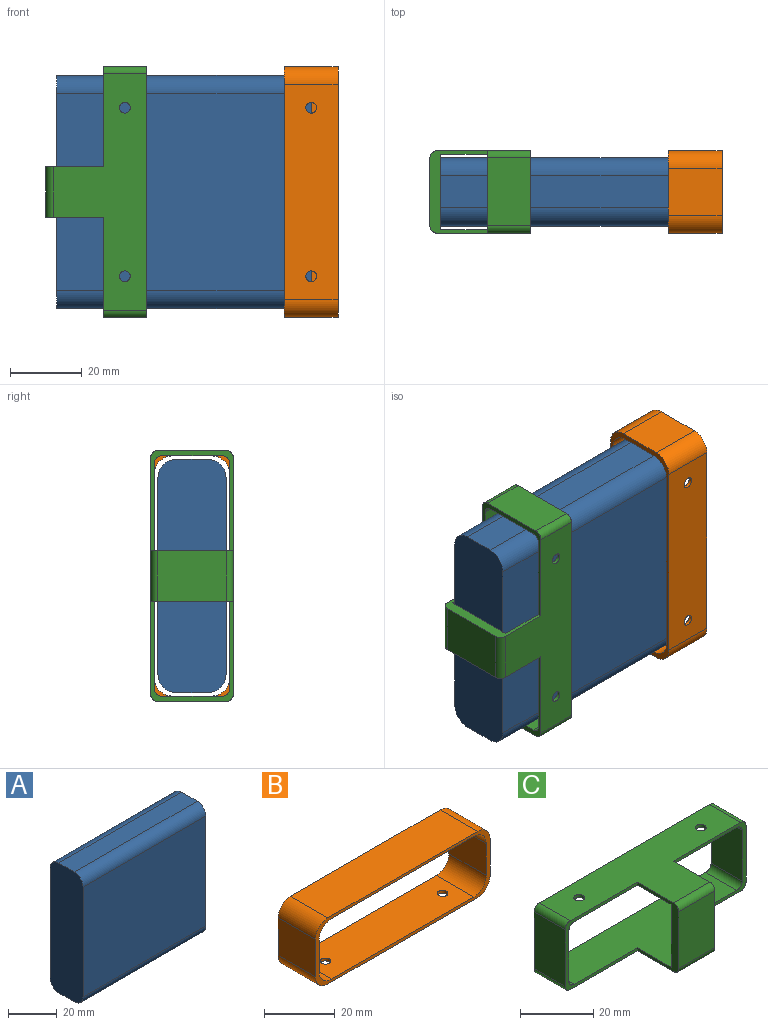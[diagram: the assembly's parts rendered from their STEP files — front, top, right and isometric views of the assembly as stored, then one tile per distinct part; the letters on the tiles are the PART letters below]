
ASSEMBLY  parts=3 mates=3
PART A: 10 faces, bbox 71x19x65 mm
  f0: plane 71x9mm, normal (0,0,1), area 639mm2, adj f1,f3,f7,f9
  f1: plane 65x19mm, normal (-1,0,0), area 1213.5mm2, adj f0,f2,f4,f5,f6,f7,f8,f9
  f2: plane 71x9mm, normal (0,0,-1), area 639mm2, adj f1,f3,f6,f8
  f3: plane 65x19mm, normal (1,0,0), area 1213.5mm2, adj f0,f2,f4,f5,f6,f7,f8,f9
  f4: plane 71x55mm, normal (0,-1,0), area 3905mm2, adj f1,f3,f8,f9
  f5: plane 71x55mm, normal (0,1,0), area 3905mm2, adj f1,f3,f6,f7
  f6: cylinder r=5mm len=71mm, axis (1,0,0), area 557.6mm2, adj f1,f2,f3,f5
  f7: cylinder r=5mm len=71mm, axis (-1,0,0), area 557.6mm2, adj f0,f1,f3,f5
  f8: cylinder r=5mm len=71mm, axis (-1,0,0), area 557.6mm2, adj f1,f2,f3,f4
  f9: cylinder r=5mm len=71mm, axis (1,0,0), area 557.6mm2, adj f0,f1,f3,f4
PART B: 20 faces, bbox 70x15x23 mm
  f0: plane 60x15mm, normal (0,0,1), area 900mm2, adj f8,f9,f14,f17
  f1: plane 15x13mm, normal (-1,0,0), area 195mm2, adj f8,f9,f14,f15
  f2: plane 60x15mm, normal (0,0,-1), area 885.9mm2, adj f8,f9,f15,f16,f18,f19
  f3: plane 15x11mm, normal (1,0,0), area 165mm2, adj f8,f9,f10,f13
  f4: plane 57x15mm, normal (0,0,-1), area 855mm2, adj f8,f9,f10,f11
  f5: plane 15x11mm, normal (-1,0,0), area 165mm2, adj f8,f9,f11,f12
  f6: plane 57x15mm, normal (0,0,1), area 840.9mm2, adj f8,f9,f12,f13,f18,f19
  f7: plane 15x13mm, normal (1,0,0), area 195mm2, adj f8,f9,f16,f17
  f8: plane 70x23mm, normal (0,-1,0), area 203mm2, adj f0,f1,f2,f3,f4,f5,f6,f7
  f9: plane 70x23mm, normal (0,1,0), area 203mm2, adj f0,f1,f2,f3,f4,f5,f6,f7
  f10: cylinder r=5mm len=15mm, axis (0,1,0), area 117.8mm2, adj f3,f4,f8,f9
  f11: cylinder r=5mm len=15mm, axis (0,-1,0), area 117.8mm2, adj f4,f5,f8,f9
  f12: cylinder r=5mm len=15mm, axis (0,1,0), area 117.8mm2, adj f5,f6,f8,f9
  f13: cylinder r=5mm len=15mm, axis (0,-1,0), area 117.8mm2, adj f3,f6,f8,f9
  f14: cylinder r=5mm len=15mm, axis (0,-1,0), area 117.8mm2, adj f0,f1,f8,f9
  f15: cylinder r=5mm len=15mm, axis (0,1,0), area 117.8mm2, adj f1,f2,f8,f9
  f16: cylinder r=5mm len=15mm, axis (0,-1,0), area 117.8mm2, adj f2,f7,f8,f9
  f17: cylinder r=5mm len=15mm, axis (0,1,0), area 117.8mm2, adj f0,f7,f8,f9
  f18: cylinder r=1.5mm len=3mm, axis (0,0,1), area 9.4mm2, adj f2,f6
  f19: cylinder r=1.5mm len=3mm, axis (0,0,1), area 9.4mm2, adj f2,f6
PART C: 27 faces, bbox 70x28x23 mm
  f0: plane 21x14mm, normal (0,1,0), area 294mm2, adj f6,f8,f12,f14
  f1: plane 19x14mm, normal (0,-1,0), area 266mm2, adj f12,f14,f17,f18
  f2: plane 66x26mm, normal (0,0,1), area 973.9mm2, adj f10,f11,f12,f13,f14,f15,f16,f18
  f3: plane 19x12mm, normal (-1,0,0), area 228mm2, adj f10,f11,f23,f24
  f4: plane 66x26mm, normal (0,0,-1), area 988mm2, adj f10,f11,f12,f13,f14,f17,f24,f25
  f5: plane 17x12mm, normal (1,0,0), area 204mm2, adj f10,f11,f19,f22
  f6: plane 63x25mm, normal (0,0,-1), area 923.9mm2, adj f0,f10,f11,f12,f13,f14,f15,f16
  f7: plane 17x12mm, normal (-1,0,0), area 204mm2, adj f10,f13,f20,f21
  f8: plane 63x25mm, normal (0,0,1), area 938mm2, adj f0,f10,f11,f12,f13,f14,f21,f22
  f9: plane 19x12mm, normal (1,0,0), area 228mm2, adj f10,f13,f25,f26
  f10: plane 70x23mm, normal (0,1,0), area 203mm2, adj f2,f3,f4,f5,f6,f7,f8,f9
  f11: plane 28x23mm, normal (0,-1,0), area 87.5mm2, adj f2,f3,f4,f5,f6,f8,f12,f19
  f12: plane 23x16mm, normal (-1,0,0), area 93.3mm2, adj f0,f1,f2,f4,f6,f8,f11,f17
  f13: plane 28x23mm, normal (0,-1,0), area 87.5mm2, adj f2,f4,f6,f7,f8,f9,f14,f20
  f14: plane 23x16mm, normal (1,0,0), area 93.3mm2, adj f0,f1,f2,f4,f6,f8,f13,f17
  f15: cylinder r=1.5mm len=3mm, axis (0,0,-1), area 9.4mm2, adj f2,f6
  f16: cylinder r=1.5mm len=3mm, axis (0,0,-1), area 9.4mm2, adj f2,f6
  f17: cylinder r=2mm len=14mm, axis (-1,0,0), area 44mm2, adj f1,f4,f12,f14
  f18: cylinder r=2mm len=14mm, axis (1,0,0), area 44mm2, adj f1,f2,f12,f14
  f19: cylinder r=2mm len=12mm, axis (0,1,0), area 37.7mm2, adj f5,f6,f10,f11
  f20: cylinder r=2mm len=12mm, axis (0,-1,0), area 37.7mm2, adj f6,f7,f10,f13
  f21: cylinder r=2mm len=12mm, axis (0,1,0), area 37.7mm2, adj f7,f8,f10,f13
  f22: cylinder r=2mm len=12mm, axis (0,-1,0), area 37.7mm2, adj f5,f8,f10,f11
  f23: cylinder r=2mm len=12mm, axis (0,-1,0), area 37.7mm2, adj f2,f3,f10,f11
  f24: cylinder r=2mm len=12mm, axis (0,1,0), area 37.7mm2, adj f3,f4,f10,f11
  f25: cylinder r=2mm len=12mm, axis (0,-1,0), area 37.7mm2, adj f4,f9,f10,f13
  f26: cylinder r=2mm len=12mm, axis (0,1,0), area 37.7mm2, adj f2,f9,f10,f13
PLACE A t=(7.92,-2.02,14.29)mm
PLACE B rot(axis=(-0.58,-0.58,-0.58),120deg) t=(20.99,-5.08,16.53)mm
PLACE C rot(axis=(0.58,0.58,-0.58),120deg) t=(-32.51,-15.05,-11.62)mm
MATE slider C.f0 <-> A.f1  axis (1,0,0) through (-57.51,-11.52,7.98)mm
MATE slider B.f6 <-> A.f4  axis (0,1,0) through (13.49,-22.02,7.98)mm
MATE slider B.f3 <-> A.f2  axis (0,0,1) through (13.49,-11.52,-25.52)mm
